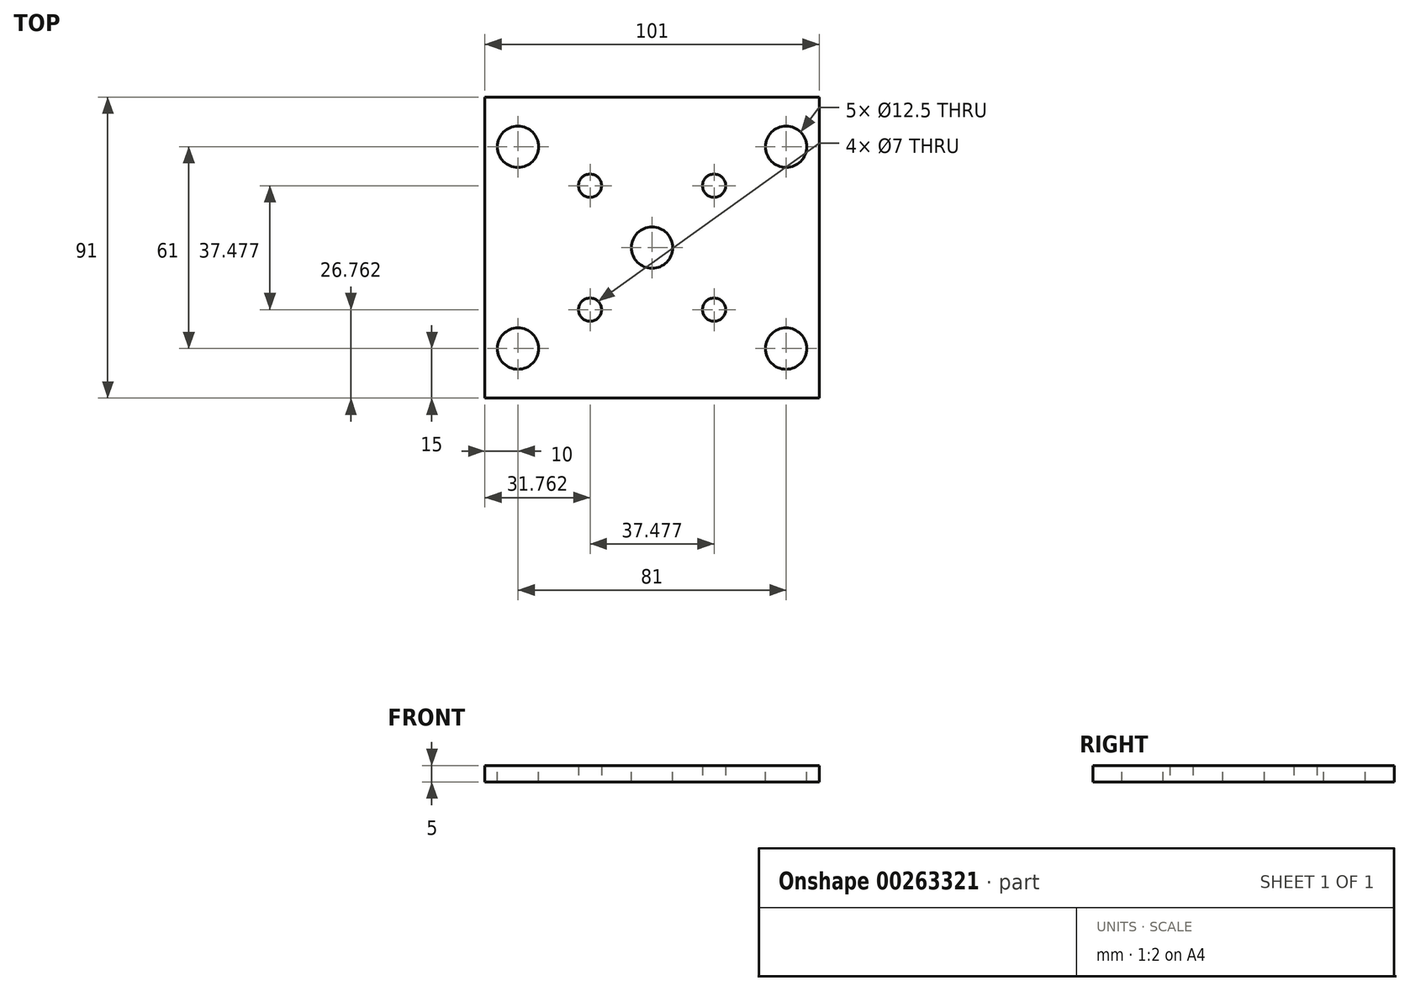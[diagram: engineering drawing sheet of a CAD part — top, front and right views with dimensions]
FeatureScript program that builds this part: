
annotation { "Feature Type Name" : "Feature", "Feature Type Description" : "" }
export const myFeature = defineFeature(function(context is Context, id is Id, definition is map)
    precondition{}
    {
        {
            var Q0;
            Q0=qCreatedBy(makeId("Top.planeOp"),FACE);
            var sketch = newSketch(context, id + "F0", { "sketchPlane" : qUnion([Q0])});
            skLineSegment(sketch, "E0", {"start": v(-50.5, 0) * mm, "end": v(-50.5, -91) * mm});
            skLineSegment(sketch, "E1", {"start": v(-50.5, -91) * mm, "end": v(50.5, -91) * mm});
            skLineSegment(sketch, "E2", {"start": v(50.5, -91) * mm, "end": v(50.5, 0) * mm});
            skLineSegment(sketch, "E3", {"start": v(50.5, 0) * mm, "end": v(-50.5, 0) * mm});
            skSolve(sketch);
        }
        {
            var Q0;
            Q0=qSketchRegion(id+"F0",true);
            extrude(context, id + "F1", {"entities" : qUnion([Q0]), "oppositeDirection" : true, "depth" : 5 * mm});
        }
        {
            var Q0;
            Q0=makeQuery(id+"F1.opExtrude","CAP_FACE",FACE,{"disambiguationData":[OSD([sQuery(id+"F0.wireOp",EDGE,"E0"),sQuery(id+"F0.wireOp",EDGE,"E1"),sQuery(id+"F0.wireOp",EDGE,"E2"),sQuery(id+"F0.wireOp",EDGE,"E3")])],"isStart":true});
            var sketch = newSketch(context, id + "F2", { "sketchPlane" : qUnion([Q0])});
            skPoint(sketch, "E4", {"position": v(-40.5, -15) * mm});
            skPoint(sketch, "E5", {"position": v(-40.5, -76) * mm});
            skPoint(sketch, "E6", {"position": v(40.5, -76) * mm});
            skPoint(sketch, "E7", {"position": v(40.5, -15) * mm});
            skPoint(sketch, "E8", {"position": v(0, -45.5) * mm});
            skPoint(sketch, "E8.positionSnap0", {"position": v(0, -91) * mm});
            skSolve(sketch);
        }
        {
            var Q0;
            Q0=sQuery(id+"F2.wireOp",VERTEX,"E5");
            var Q1;
            Q1=sQuery(id+"F2.wireOp",VERTEX,"E6");
            var Q2;
            Q2=sQuery(id+"F2.wireOp",VERTEX,"E7");
            var Q3;
            Q3=sQuery(id+"F2.wireOp",VERTEX,"E4");
            var Q4;
            Q4=sQuery(id+"F2.wireOp",VERTEX,"E8");
            var Q5;
            Q5=makeQuery(id+"F1.opExtrude","SWEPT_BODY",BODY,{"disambiguationData":[OSD([sQuery(id+"F0.wireOp",EDGE,"E0"),sQuery(id+"F0.wireOp",EDGE,"E1"),sQuery(id+"F0.wireOp",EDGE,"E2"),sQuery(id+"F0.wireOp",EDGE,"E3")])]});
            hole(context, id + "F3", {"style" : HoleStyle.SIMPLE, "endStyle" : HoleEndStyle.THROUGH, "holeDiameter" : 12.5 * mm, "tappedDepth" : 12 * mm, "tapClearance" : 3, "locations" : qUnion([Q0, Q1, Q2, Q3, Q4]), "scope" : qUnion([Q5])});
        }
        {
            var Q0;
            Q0=makeQuery(id+"F1.opExtrude","CAP_FACE",FACE,{"disambiguationData":[OSD([sQuery(id+"F0.wireOp",EDGE,"E0"),sQuery(id+"F0.wireOp",EDGE,"E1"),sQuery(id+"F0.wireOp",EDGE,"E2"),sQuery(id+"F0.wireOp",EDGE,"E3")])],"isStart":false});
            var sketch = newSketch(context, id + "F4", { "sketchPlane" : qUnion([Q0])});
            skLineSegment(sketch, "E9", {"start": v(0, 0) * mm, "end": v(0, 91) * mm, "construction": true});
            skLineSegment(sketch, "E10", {"start": v(50.5, 45.5) * mm, "end": v(-50.5, 45.5) * mm, "construction": true});
            skPoint(sketch, "E11", {"position": v(0, 45.5) * mm});
            skPoint(sketch, "E12", {"position": v(-18.74, 64.24) * mm});
            skPoint(sketch, "E13", {"position": v(-18.74, 26.76) * mm});
            skPoint(sketch, "E14", {"position": v(18.74, 64.24) * mm});
            skPoint(sketch, "E15", {"position": v(18.74, 26.76) * mm});
            skSolve(sketch);
        }
        {
            var Q0;
            Q0=sQuery(id+"F4.wireOp",VERTEX,"E12");
            var Q1;
            Q1=sQuery(id+"F4.wireOp",VERTEX,"E13");
            var Q2;
            Q2=sQuery(id+"F4.wireOp",VERTEX,"E15");
            var Q3;
            Q3=sQuery(id+"F4.wireOp",VERTEX,"E14");
            var Q4;
            Q4=makeQuery(id+"F1.opExtrude","SWEPT_BODY",BODY,{"disambiguationData":[OSD([sQuery(id+"F0.wireOp",EDGE,"E0"),sQuery(id+"F0.wireOp",EDGE,"E1"),sQuery(id+"F0.wireOp",EDGE,"E2"),sQuery(id+"F0.wireOp",EDGE,"E3")])]});
            hole(context, id + "F5", {"style" : HoleStyle.SIMPLE, "endStyle" : HoleEndStyle.THROUGH, "holeDiameter" : 7 * mm, "tappedDepth" : 12 * mm, "tapClearance" : 3, "locations" : qUnion([Q0, Q1, Q2, Q3]), "scope" : qUnion([Q4])});
        }
    });
